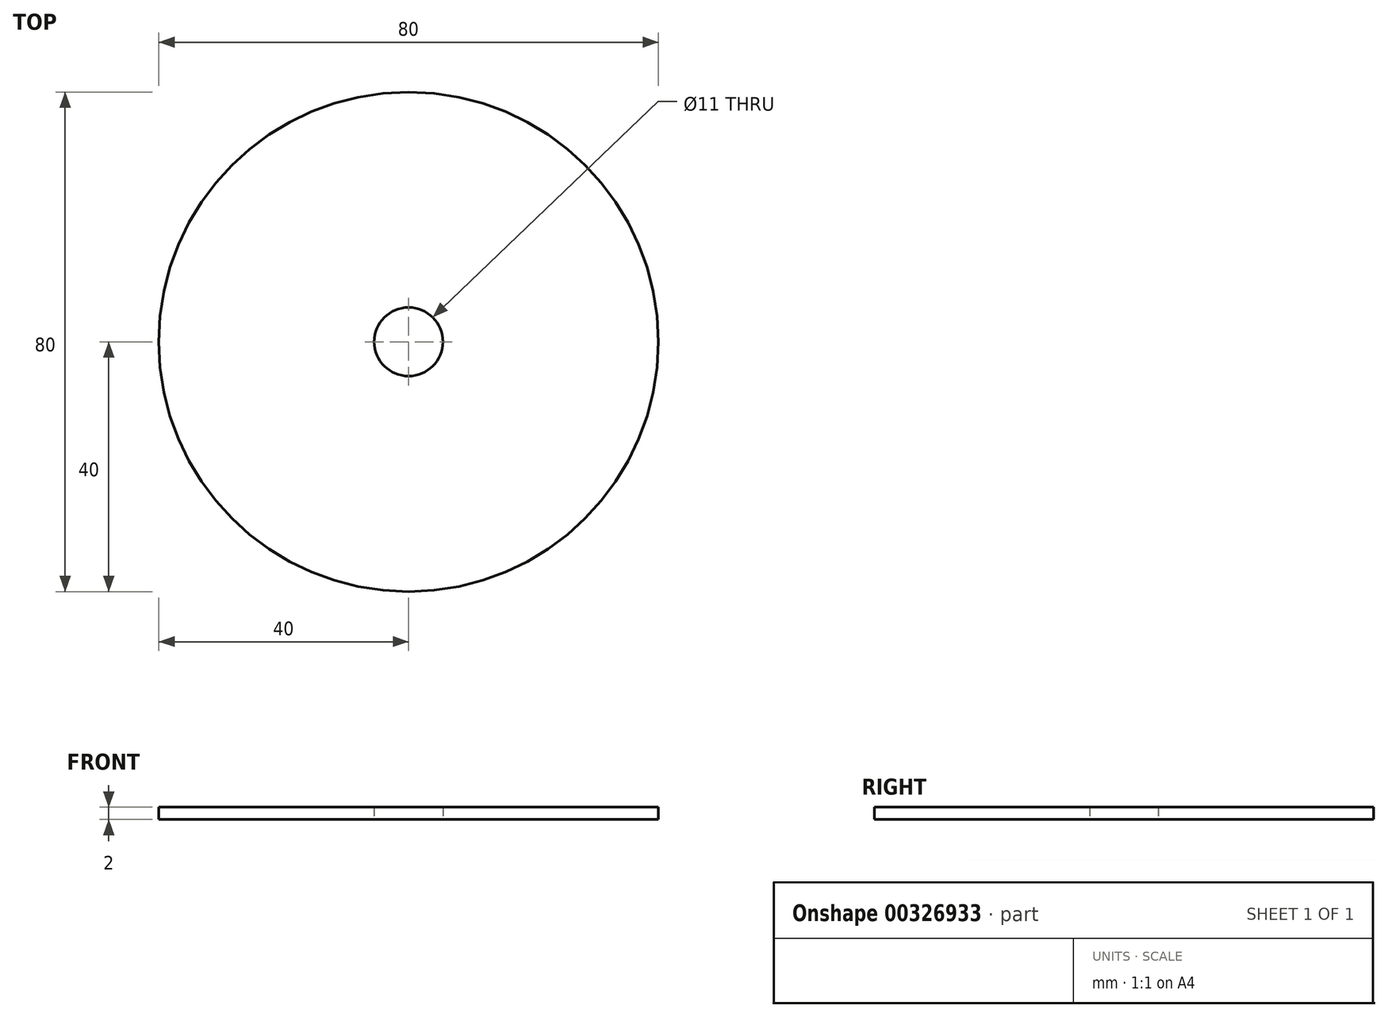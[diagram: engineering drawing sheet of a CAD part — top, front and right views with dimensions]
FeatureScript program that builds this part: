
annotation { "Feature Type Name" : "Feature", "Feature Type Description" : "" }
export const myFeature = defineFeature(function(context is Context, id is Id, definition is map)
    precondition{}
    {
        {
            var Q0;
            Q0=qCreatedBy(makeId("Top.planeOp"),FACE);
            var sketch = newSketch(context, id + "F0", { "sketchPlane" : qUnion([Q0])});
            skCircle(sketch, "E0", {"center": v(0, 0) * mm, "radius": 40 * mm});
            skCircle(sketch, "E1", {"center": v(0, 0) * mm, "radius": 5.5 * mm});
            skSolve(sketch);
        }
        {
            var Q0;
            Q0 = qSketchRegion(id + "F0", true);
            extrude(context, id + "F1", {"entities" : qUnion([Q0]), "depth" : 2 * mm});
        }
    });
